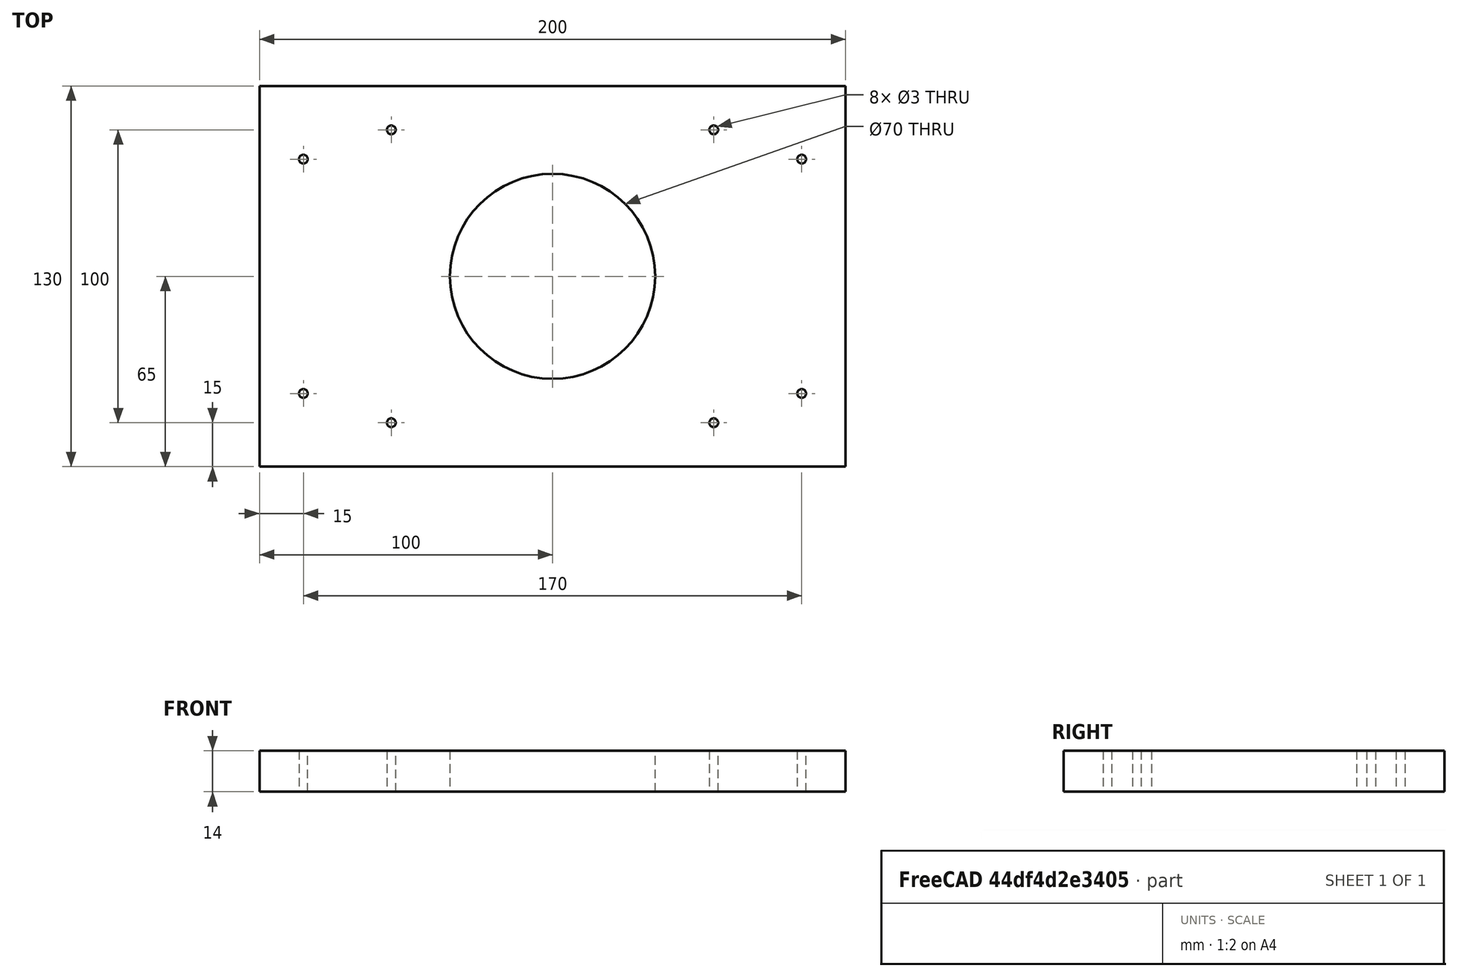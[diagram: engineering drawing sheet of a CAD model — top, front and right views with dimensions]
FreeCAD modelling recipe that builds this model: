
FCSTD DOCUMENT  (FreeCAD 0.19R24276 (Git))
Label: Plate_200x130_d70_4napravl_4_krep_otv
License: All rights reserved
LicenseURL: http://en.wikipedia.org/wiki/All_rights_reserved
objects: Sketcher::SketchObject×1, PartDesign::Pad×1, PartDesign::Body×1
note: 4 computed .brp shape members not serialized (recipe doc carries the construction recipe); baked Part::Feature solids carry a one-line shape summary decoded from their .brp

FEATURE [Sketcher::SketchObject] Sketch
  FullyConstrained = true
  MapMode = 5
  Support = -> [XY_Plane]
  sketch-geometry (21):
    g0: LineSegment StartX=0 StartY=0 StartZ=0 EndX=200 EndY=0 EndZ=0
    g1: LineSegment StartX=200 StartY=0 StartZ=0 EndX=200 EndY=130 EndZ=0
    g2: LineSegment StartX=200 StartY=130 StartZ=0 EndX=0 EndY=130 EndZ=0
    g3: LineSegment StartX=0 StartY=130 StartZ=0 EndX=0 EndY=0 EndZ=0
    g4: Circle CenterX=100 CenterY=65 CenterZ=0 NormalX=0 NormalY=0 NormalZ=1 AngleXU=0 Radius=35
    g5: Circle CenterX=45 CenterY=115 CenterZ=0 NormalX=0 NormalY=0 NormalZ=1 AngleXU=0 Radius=1.5
    g6: Circle CenterX=45 CenterY=15 CenterZ=0 NormalX=0 NormalY=0 NormalZ=1 AngleXU=0 Radius=1.5
    g7: Circle CenterX=155 CenterY=115 CenterZ=0 NormalX=0 NormalY=0 NormalZ=1 AngleXU=0 Radius=1.5
    g8: Circle CenterX=155 CenterY=15 CenterZ=0 NormalX=0 NormalY=0 NormalZ=1 AngleXU=0 Radius=1.5
    g9: LineSegment StartX=45 StartY=15 StartZ=0 EndX=45 EndY=115 EndZ=0
    g10: LineSegment StartX=45 StartY=15 StartZ=0 EndX=155 EndY=15 EndZ=0
    g11: LineSegment StartX=155 StartY=115 StartZ=0 EndX=155 EndY=15 EndZ=0
    g12: LineSegment StartX=45 StartY=115 StartZ=0 EndX=155 EndY=115 EndZ=0
    g13: Circle CenterX=15 CenterY=105 CenterZ=0 NormalX=0 NormalY=0 NormalZ=1 AngleXU=0 Radius=1.5
    g14: Circle CenterX=15 CenterY=25 CenterZ=0 NormalX=0 NormalY=0 NormalZ=1 AngleXU=0 Radius=1.5
    g15: Circle CenterX=185 CenterY=105 CenterZ=0 NormalX=0 NormalY=0 NormalZ=1 AngleXU=0 Radius=1.5
    g16: Circle CenterX=185 CenterY=25 CenterZ=0 NormalX=0 NormalY=0 NormalZ=1 AngleXU=0 Radius=1.5
    g17: LineSegment StartX=15 StartY=105 StartZ=0 EndX=15 EndY=25 EndZ=0
    g18: LineSegment StartX=185 StartY=105 StartZ=0 EndX=185 EndY=25 EndZ=0
    g19: LineSegment StartX=15 StartY=25 StartZ=0 EndX=185 EndY=25 EndZ=0
    g20: LineSegment StartX=185 StartY=105 StartZ=0 EndX=15 EndY=105 EndZ=0
  constraints (52):
    c: Coincident(g0,g1)
    c: Coincident(g1,g2)
    c: Coincident(g2,g3)
    c: Coincident(g3,g0)
    c: Horizontal(g0)
    c: Horizontal(g2)
    c: Vertical(g1)
    c: Vertical(g3)
    c: Coincident(g0,g-1)
    c: DistanceY(g1,g1) = 130
    c: DistanceX(g0,g0) = 200
    c: Symmetric(g2,g0,g4)
    c: Diameter(g4) = 70
    c: DistanceX(g0,g6) = 45
    c: Coincident(g9,g6)
    c: Coincident(g9,g5)
    c: Vertical(g9)
    c: Coincident(g10,g6)
    c: Coincident(g10,g8)
    c: Horizontal(g10)
    c: Coincident(g11,g7)
    c: Coincident(g11,g8)
    c: Vertical(g11)
    c: Coincident(g12,g5)
    c: Coincident(g12,g7)
    c: Horizontal(g12)
    c: Symmetric(g7,g6,g4)
    c: DistanceY(g0,g6) = 15
    c: Coincident(g17,g13)
    c: Coincident(g17,g14)
    c: Coincident(g18,g15)
    c: Coincident(g18,g16)
    c: Vertical(g18)
    c: Coincident(g19,g14)
    c: Coincident(g19,g16)
    c: Vertical(g17)
    c: Horizontal(g19)
    c: Coincident(g20,g15)
    c: Coincident(g20,g13)
    c: Horizontal(g20)
    c: Diameter(g5) = 3
    c: Equal(g5,g6)
    c: Equal(g5,g8)
    c: Equal(g5,g7)
    c: Diameter(g13) = 3
    c: Equal(g13,g14)
    c: Equal(g13,g15)
    c: Equal(g13,g16)
    c: DistanceY(g13,g2) = 25
    c: DistanceY(g0,g14) = 25
    c: DistanceX(g0,g14) = 15
    c: DistanceX(g16,g0) = 15
FEATURE [PartDesign::Pad] Pad
  Direction = (1,1,1)
  Length = 14
  Length2 = 100
  Profile = -> Sketch
  Type = 0
FEATURE [PartDesign::Body] Body
  Group = -> [Sketch,Pad]
  Origin = -> Origin
  Tip = -> Pad
